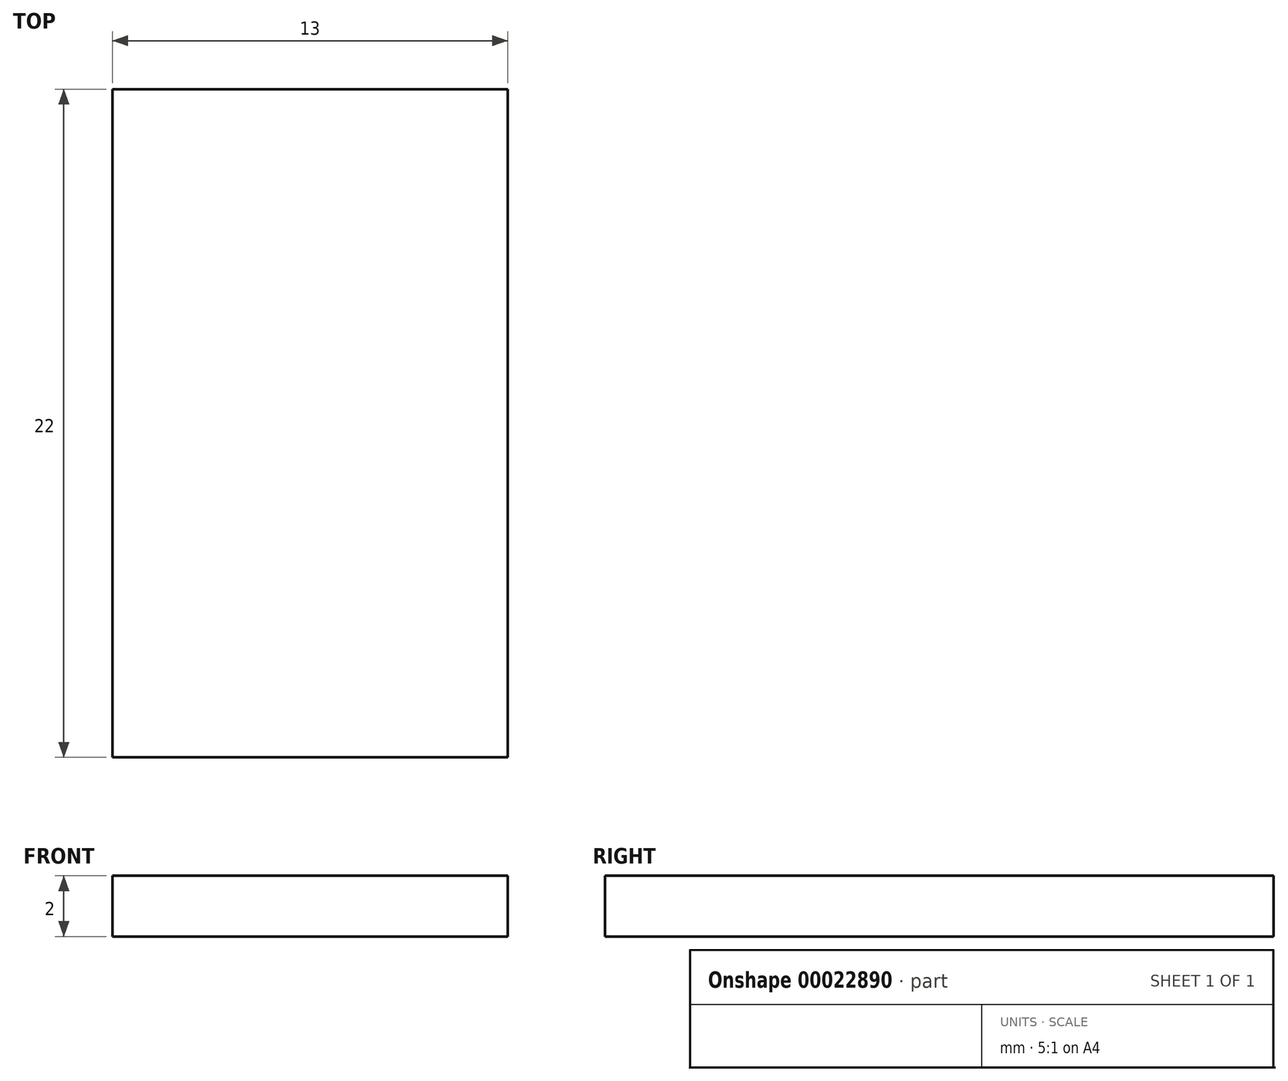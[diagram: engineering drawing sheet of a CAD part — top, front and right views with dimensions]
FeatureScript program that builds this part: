
annotation { "Feature Type Name" : "Feature", "Feature Type Description" : "" }
export const myFeature = defineFeature(function(context is Context, id is Id, definition is map)
    precondition{}
    {
        {
            var Q0;
            Q0=qCreatedBy(makeId("Top.planeOp"),FACE);
            var sketch = newSketch(context, id + "F0", { "sketchPlane" : qUnion([Q0])});
            skLineSegment(sketch, "E0.bottom", {"start": v(-6.5, 13) * mm, "end": v(6.5, 13) * mm});
            skLineSegment(sketch, "E0.top", {"start": v(-6.5, -9) * mm, "end": v(6.5, -9) * mm});
            skLineSegment(sketch, "E0.left", {"start": v(-6.5, 13) * mm, "end": v(-6.5, -9) * mm});
            skLineSegment(sketch, "E0.right", {"start": v(6.5, 13) * mm, "end": v(6.5, -9) * mm});
            skSolve(sketch);
        }
        {
            var Q0;
            Q0=makeQuery(id+"F0.imprint","IMPRINT",FACE,{"disambiguationData":[TD([[makeQuery(id+"F0.imprint","IMPRINT",EDGE,{"derivedFrom":sQuery(id+"F0.wireOp",EDGE,"E0.bottom")}),-1.0]])]});
            extrude(context, id + "F1", {"entities" : qUnion([Q0]), "depth" : 2 * mm});
        }
    });
